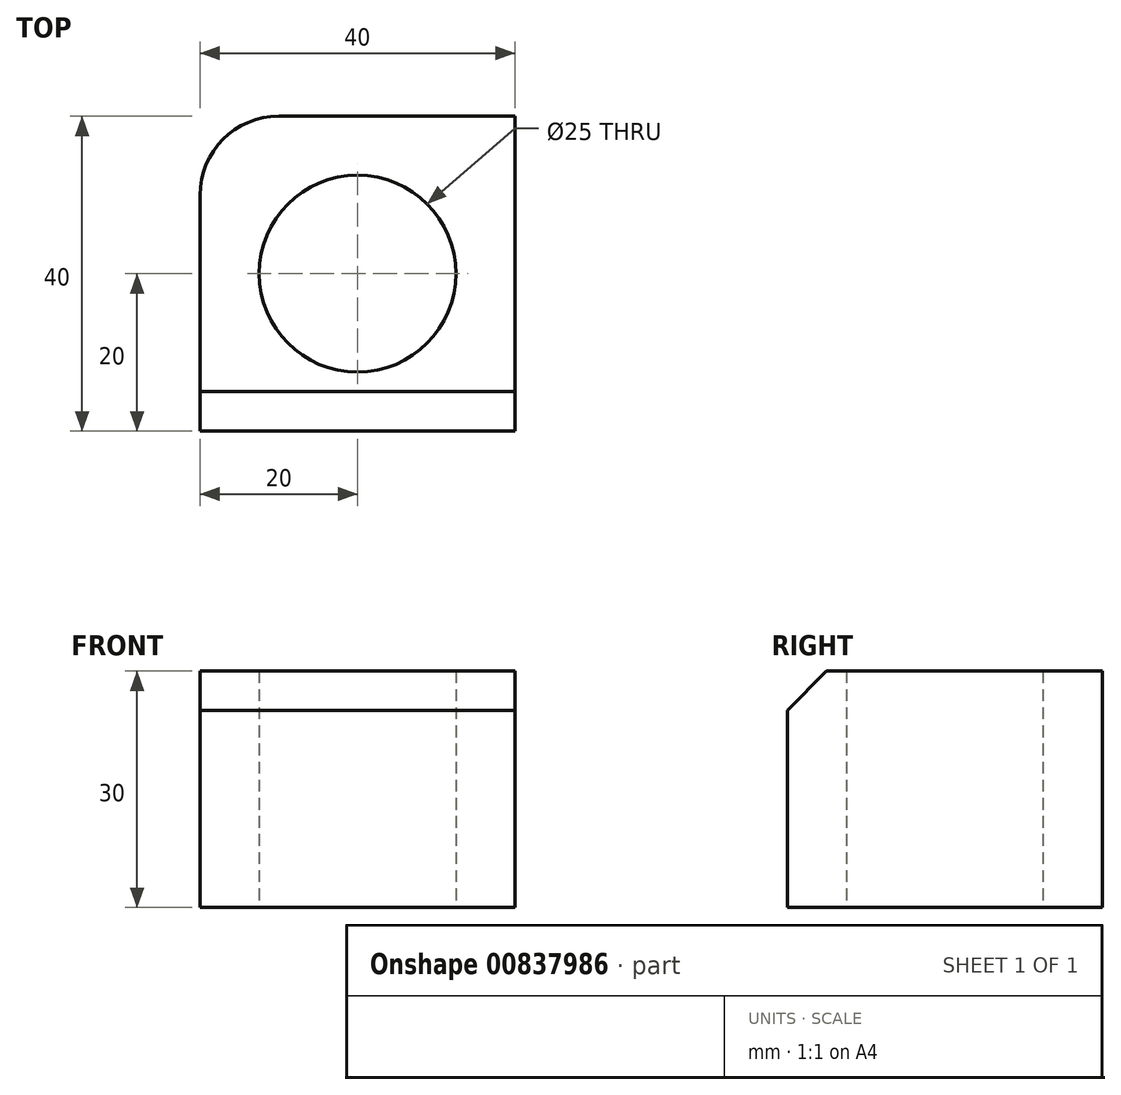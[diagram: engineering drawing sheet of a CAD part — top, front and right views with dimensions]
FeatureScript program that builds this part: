
annotation { "Feature Type Name" : "Feature", "Feature Type Description" : "" }
export const myFeature = defineFeature(function(context is Context, id is Id, definition is map)
    precondition{}
    {
        {
            var Q0;
            Q0=qCreatedBy(makeId("Top.planeOp"),FACE);
            var sketch = newSketch(context, id + "F0", { "sketchPlane" : qUnion([Q0])});
            skLineSegment(sketch, "E0", {"start": v(0, 0) * mm, "end": v(0, 10) * mm});
            skLineSegment(sketch, "E1", {"start": v(10, 20) * mm, "end": v(40, 20) * mm});
            skLineSegment(sketch, "E2", {"start": v(40, 20) * mm, "end": v(40, 0) * mm});
            skLineSegment(sketch, "E3", {"start": v(40, 0) * mm, "end": v(0, 0) * mm, "construction": true});
            skLineSegment(sketch, "E4.MirrorCS", {"start": v(40, -20) * mm, "end": v(40, 0) * mm});
            skLineSegment(sketch, "E5.MirrorCS", {"start": v(0, -20) * mm, "end": v(40, -20) * mm});
            skLineSegment(sketch, "E6.MirrorCS", {"start": v(0, 0) * mm, "end": v(0, -20) * mm});
            skCircle(sketch, "E7", {"center": v(20, 0) * mm, "radius": 12.5 * mm});
            skPoint(sketch, "E8.visualSharp", {"position": v(0, 20) * mm});
            skArc(sketch, "E8.filletArc", {"start": v(10, 20) * mm, "mid": v(2.93, 17.07) * mm, "end": v(0, 10) * mm});
            skSolve(sketch);
        }
        {
            var Q0;
            Q0=makeQuery(id+"F0.imprint","IMPRINT",FACE,{"disambiguationData":[TD([[makeQuery(id+"F0.imprint","IMPRINT",EDGE,{"derivedFrom":sQuery(id+"F0.wireOp",EDGE,"E0")}),-1.0]])]});
            extrude(context, id + "F1", {"entities" : qUnion([Q0]), "depth" : 30 * mm, "offsetDistance" : 25 * mm});
        }
        {
            var Q0;
            Q0=makeQuery(id+"F1.opExtrude","CAP_EDGE",EDGE,{"disambiguationData":[OSD([sQuery(id+"F0.wireOp",EDGE,"E5.MirrorCS")])],"isStart":false});
            chamfer(context, id + "F2", {"entities" : qUnion([Q0]), "width" : 5 * mm, "tangentPropagation" : true});
        }
    });
